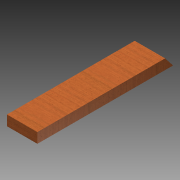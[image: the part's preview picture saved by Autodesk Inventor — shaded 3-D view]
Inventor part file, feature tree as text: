
AUTODESK INVENTOR PART (.ipt)
format: ipt  version: 2014 (Build 180170000, 170)  size: 86,016 bytes
history: native  units: in
note: dims shown in document units (in); Inventor stores cm internally (conversion verified against a paired STEP export)
features: extrude x1, sketch x1
ambient origin geometry x8: Origin, YZ Plane, XZ Plane, XY Plane, X Axis, Y Axis, Z Axis, Center Point
bodies: Solid1 (feature_tree)
feature tree (2):
  extrude  "Extrusion1"  Depth=20.0in
  sketch  "Sketch1"  dims[d0=1.4961in d1=20.0in d2=0.3573in d3=4.4882in d4=0.0in]
